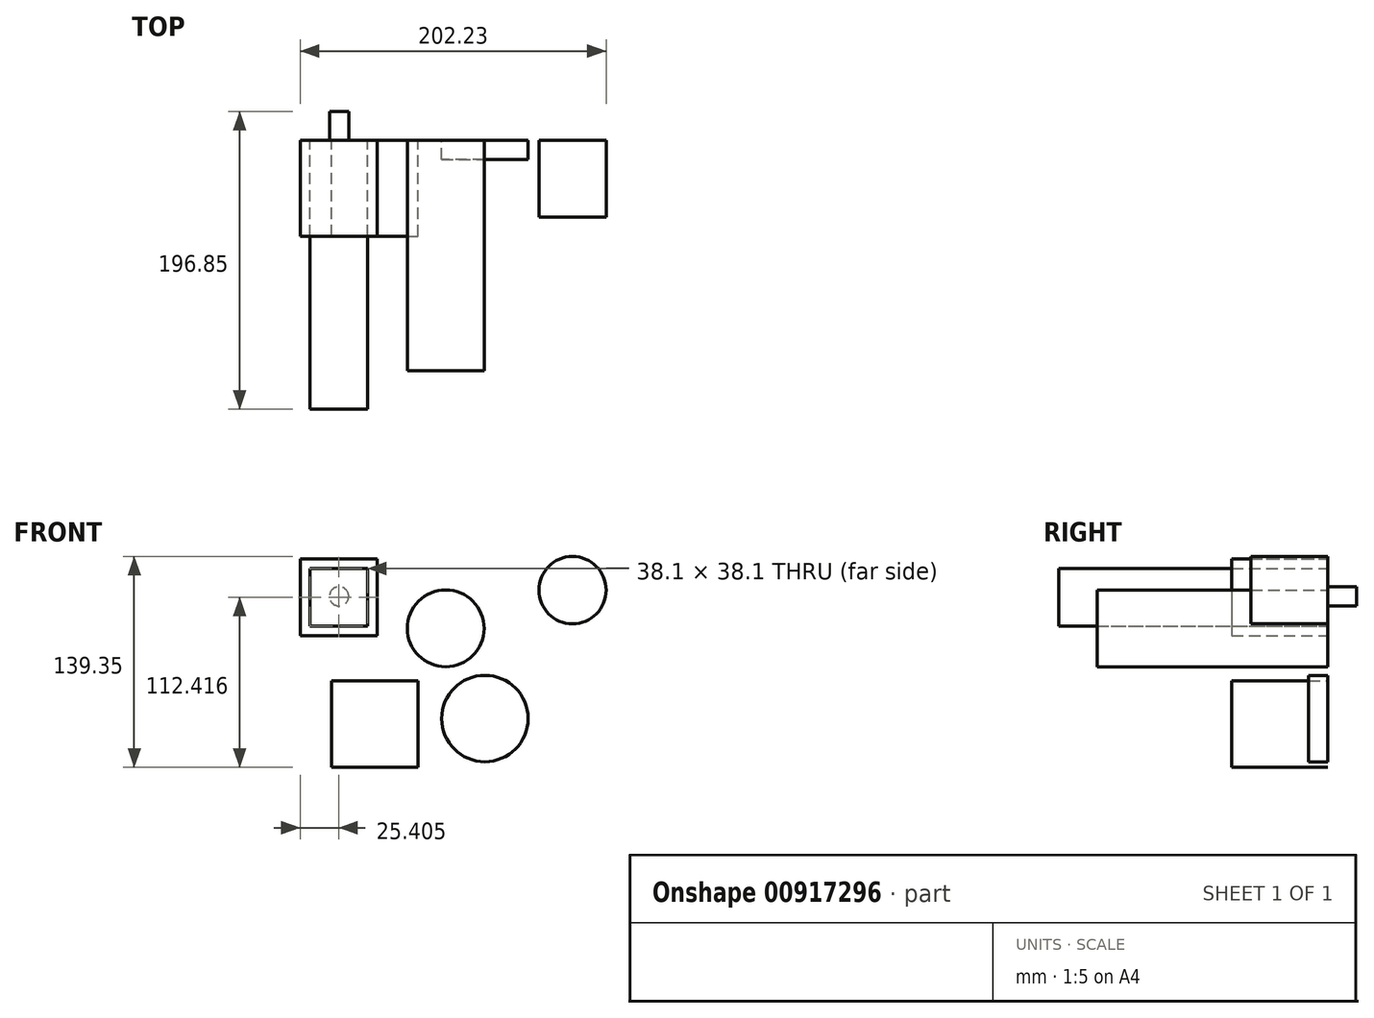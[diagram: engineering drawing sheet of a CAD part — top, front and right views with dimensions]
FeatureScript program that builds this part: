
annotation { "Feature Type Name" : "Feature", "Feature Type Description" : "" }
export const myFeature = defineFeature(function(context is Context, id is Id, definition is map)
    precondition{}
    {
        {
            var Q0;
            Q0=qCreatedBy(makeId("Front.planeOp"),FACE);
            var sketch = newSketch(context, id + "F0", { "sketchPlane" : qUnion([Q0])});
            skCircle(sketch, "E0", {"center": v(11.34, 33.63) * mm, "radius": 25.4 * mm});
            skLineSegment(sketch, "E1.bottom", {"start": v(-64.25, -1.03) * mm, "end": v(-7.1, -1.03) * mm});
            skLineSegment(sketch, "E1.top", {"start": v(-64.25, -58.18) * mm, "end": v(-7.1, -58.18) * mm});
            skLineSegment(sketch, "E1.left", {"start": v(-64.25, -1.03) * mm, "end": v(-64.25, -58.18) * mm});
            skLineSegment(sketch, "E1.right", {"start": v(-7.1, -1.03) * mm, "end": v(-7.1, -58.18) * mm});
            skCircle(sketch, "E2", {"center": v(37.24, -25.98) * mm, "radius": 28.58 * mm});
            skLineSegment(sketch, "E3.bottom", {"start": v(-84.87, 79.64) * mm, "end": v(-34.07, 79.64) * mm});
            skLineSegment(sketch, "E3.top", {"start": v(-84.87, 28.84) * mm, "end": v(-34.07, 28.84) * mm});
            skLineSegment(sketch, "E3.left", {"start": v(-84.87, 79.64) * mm, "end": v(-84.87, 28.84) * mm});
            skLineSegment(sketch, "E3.right", {"start": v(-34.07, 79.64) * mm, "end": v(-34.07, 28.84) * mm});
            skLineSegment(sketch, "E4.bottom", {"start": v(-78.52, 73.29) * mm, "end": v(-40.42, 73.29) * mm});
            skLineSegment(sketch, "E4.top", {"start": v(-78.52, 35.19) * mm, "end": v(-40.42, 35.19) * mm});
            skLineSegment(sketch, "E4.left", {"start": v(-78.52, 73.29) * mm, "end": v(-78.52, 35.19) * mm});
            skLineSegment(sketch, "E4.right", {"start": v(-40.42, 73.29) * mm, "end": v(-40.42, 35.19) * mm});
            skCircle(sketch, "E5", {"center": v(-59.16, 54.81) * mm, "radius": 6.35 * mm});
            skLineSegment(sketch, "E6", {"start": v(-59.16, 54.81) * mm, "end": v(-59.16, 73.29) * mm, "construction": true});
            skLineSegment(sketch, "E7", {"start": v(-59.16, 54.81) * mm, "end": v(-40.42, 54.81) * mm, "construction": true});
            skCircle(sketch, "E8", {"center": v(95.13, 58.94) * mm, "radius": 22.23 * mm});
            skSolve(sketch);
        }
        {
            var Q0;
            Q0=makeQuery(id+"F0.imprint","IMPRINT",FACE,{"disambiguationData":[TD([[makeQuery(id+"F0.imprint","IMPRINT",EDGE,{"derivedFrom":sQuery(id+"F0.wireOp",EDGE,"E0")}),1.0]])]});
            extrude(context, id + "F1", {"entities" : qUnion([Q0]), "depth" : 152.4 * mm, "offsetDistance" : 25.4 * mm});
        }
        {
            var Q0;
            Q0=makeQuery(id+"F0.imprint","IMPRINT",FACE,{"disambiguationData":[TD([[makeQuery(id+"F0.imprint","IMPRINT",EDGE,{"derivedFrom":sQuery(id+"F0.wireOp",EDGE,"E2")}),1.0]])]});
            extrude(context, id + "F2", {"entities" : qUnion([Q0]), "depth" : 12.7 * mm, "offsetDistance" : 25.4 * mm});
        }
        {
            var Q0;
            Q0=makeQuery(id+"F0.imprint","IMPRINT",FACE,{"disambiguationData":[TD([[makeQuery(id+"F0.imprint","IMPRINT",EDGE,{"derivedFrom":sQuery(id+"F0.wireOp",EDGE,"E1.bottom")}),-1.0]])]});
            extrude(context, id + "F3", {"entities" : qUnion([Q0]), "depth" : 63.5 * mm, "offsetDistance" : 25.4 * mm});
        }
        {
            var Q0;
            Q0=makeQuery(id+"F0.imprint","IMPRINT",FACE,{"disambiguationData":[TD([[makeQuery(id+"F0.imprint","IMPRINT",EDGE,{"derivedFrom":sQuery(id+"F0.wireOp",EDGE,"E4.bottom")}),-1.0]])]});
            var Q1;
            Q1=makeQuery(id+"F0.imprint","IMPRINT",FACE,{"disambiguationData":[TD([[makeQuery(id+"F0.imprint","IMPRINT",EDGE,{"derivedFrom":sQuery(id+"F0.wireOp",EDGE,"E5")}),1.0]])]});
            extrude(context, id + "F4", {"entities" : qUnion([Q0, Q1]), "depth" : 177.8 * mm, "offsetDistance" : 25.4 * mm});
        }
        {
            var Q0;
            Q0=makeQuery(id+"F0.imprint","IMPRINT",FACE,{"disambiguationData":[TD([[makeQuery(id+"F0.imprint","IMPRINT",EDGE,{"derivedFrom":sQuery(id+"F0.wireOp",EDGE,"E3.bottom")}),-1.0]])]});
            extrude(context, id + "F5", {"entities" : qUnion([Q0]), "depth" : 63.5 * mm, "offsetDistance" : 25.4 * mm});
        }
        {
            var Q0;
            Q0=makeQuery(id+"F0.imprint","IMPRINT",FACE,{"disambiguationData":[TD([[makeQuery(id+"F0.imprint","IMPRINT",EDGE,{"derivedFrom":sQuery(id+"F0.wireOp",EDGE,"E5")}),1.0]])]});
            extrude(context, id + "F6", {"entities" : qUnion([Q0]), "operationType" : NewBodyOperationType.ADD, "oppositeDirection" : true, "depth" : 19.05 * mm, "offsetDistance" : 25.4 * mm});
        }
        {
            var Q0;
            Q0=makeQuery(id+"F0.imprint","IMPRINT",FACE,{"disambiguationData":[TD([[makeQuery(id+"F0.imprint","IMPRINT",EDGE,{"derivedFrom":sQuery(id+"F0.wireOp",EDGE,"E8")}),1.0]])]});
            extrude(context, id + "F7", {"entities" : qUnion([Q0]), "depth" : 50.8 * mm, "offsetDistance" : 25.4 * mm});
        }
    });
